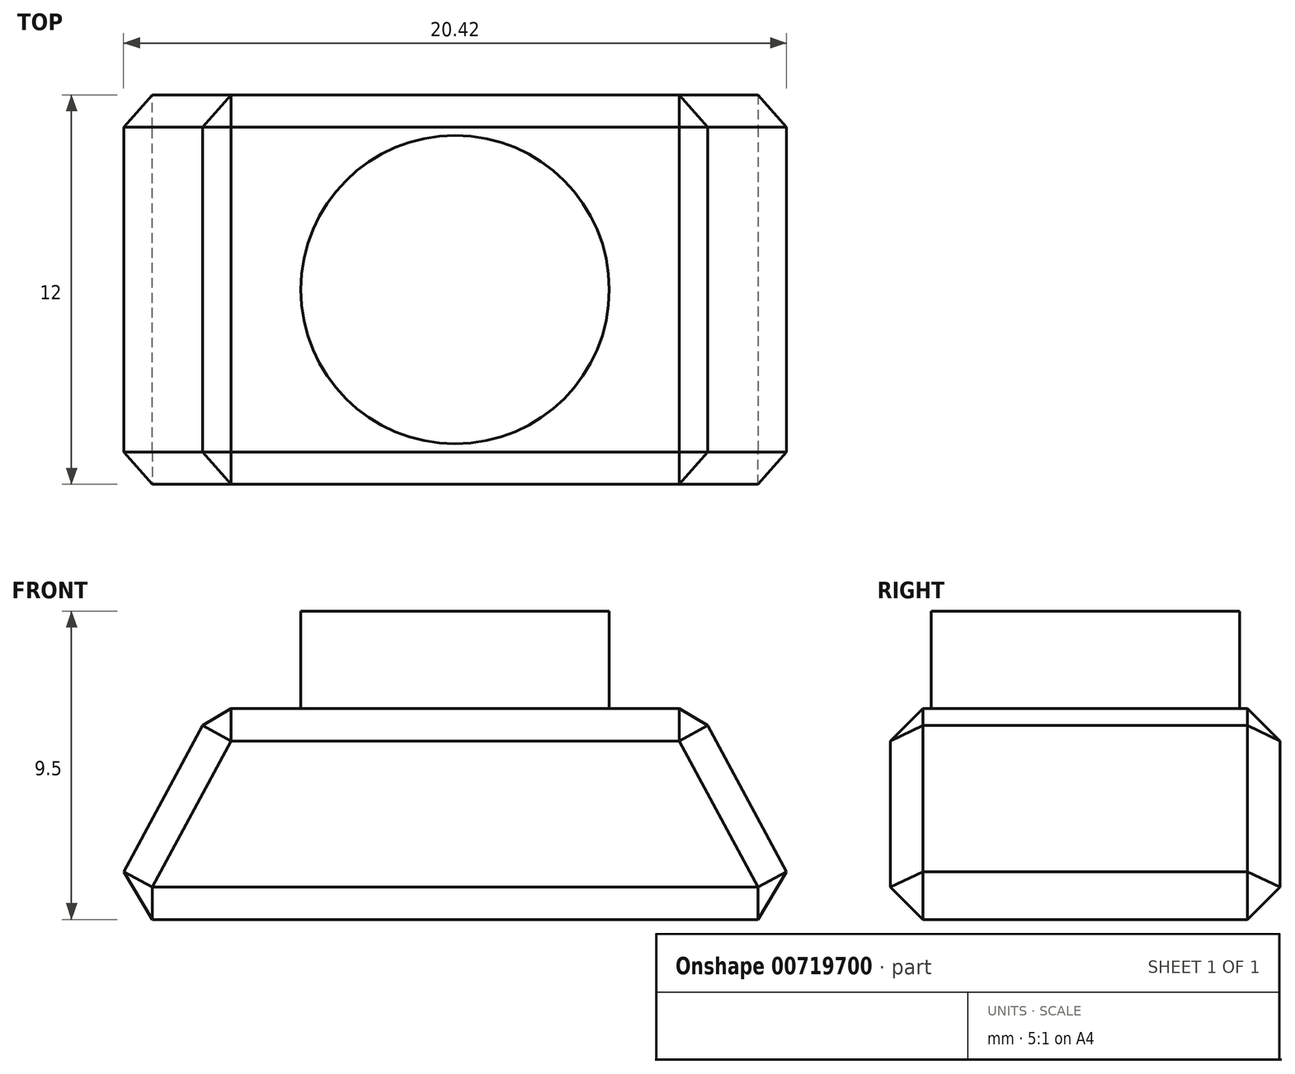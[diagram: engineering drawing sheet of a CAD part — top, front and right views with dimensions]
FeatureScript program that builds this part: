
annotation { "Feature Type Name" : "Feature", "Feature Type Description" : "" }
export const myFeature = defineFeature(function(context is Context, id is Id, definition is map)
    precondition{}
    {
        {
            var Q0;
            Q0=qCreatedBy(makeId("Top.planeOp"),FACE);
            var sketch = newSketch(context, id + "F0", { "sketchPlane" : qUnion([Q0])});
            skLineSegment(sketch, "E0.bottom", {"start": v(7.5, -6) * mm, "end": v(-7.5, -6) * mm});
            skLineSegment(sketch, "E0.top", {"start": v(7.5, 6) * mm, "end": v(-7.5, 6) * mm});
            skLineSegment(sketch, "E0.left", {"start": v(7.5, -6) * mm, "end": v(7.5, 6) * mm});
            skLineSegment(sketch, "E0.right", {"start": v(-7.5, -6) * mm, "end": v(-7.5, 6) * mm});
            skPoint(sketch, "E0.middle", {"position": v(0, 0) * mm});
            skCircle(sketch, "E1", {"center": v(0, 0) * mm, "radius": 4.75 * mm});
            skSolve(sketch);
        }
        {
            var Q0;
            Q0=makeQuery(id+"F0.imprint","IMPRINT",FACE,{"disambiguationData":[TD([[makeQuery(id+"F0.imprint","IMPRINT",EDGE,{"derivedFrom":sQuery(id+"F0.wireOp",EDGE,"E1")}),1.0]])]});
            extrude(context, id + "F1", {"entities" : qUnion([Q0]), "depth" : 3 * mm, "offsetDistance" : 25 * mm});
        }
        {
            var Q0;
            Q0=makeQuery(id+"F0.imprint","IMPRINT",FACE,{"disambiguationData":[TD([[makeQuery(id+"F0.imprint","IMPRINT",EDGE,{"derivedFrom":sQuery(id+"F0.wireOp",EDGE,"E0.bottom")}),-1.0]])]});
            cPlane(context, id + "F2", {"entities" : qUnion([Q0]), "cplaneType" : CPlaneType.OFFSET, "offset" : 6.5 * mm, "oppositeDirection" : true, "width" : 150 * mm, "height" : 150 * mm});
        }
        {
            var Q0;
            Q0=qCreatedBy(id+"F2.planeOp",FACE);
            var sketch = newSketch(context, id + "F3", { "sketchPlane" : qUnion([Q0])});
            skLineSegment(sketch, "E2.bottom", {"start": v(11, 6) * mm, "end": v(-11, 6) * mm});
            skLineSegment(sketch, "E2.top", {"start": v(11, -6) * mm, "end": v(-11, -6) * mm});
            skLineSegment(sketch, "E2.left", {"start": v(11, 6) * mm, "end": v(11, -6) * mm});
            skLineSegment(sketch, "E2.right", {"start": v(-11, 6) * mm, "end": v(-11, -6) * mm});
            skPoint(sketch, "E2.middle", {"position": v(0, 0) * mm});
            skSolve(sketch);
        }
        {
            var Q0;
            Q0=makeQuery(id+"F0.imprint","IMPRINT",FACE,{"disambiguationData":[TD([[makeQuery(id+"F0.imprint","IMPRINT",EDGE,{"derivedFrom":sQuery(id+"F0.wireOp",EDGE,"E1")}),1.0]])]});
            var sketch = newSketch(context, id + "F4", { "sketchPlane" : qUnion([Q0])});
            skLineSegment(sketch, "E3.bottom", {"start": v(7.5, 6) * mm, "end": v(-7.5, 6) * mm});
            skLineSegment(sketch, "E3.top", {"start": v(7.5, -6) * mm, "end": v(-7.5, -6) * mm});
            skLineSegment(sketch, "E3.left", {"start": v(7.5, 6) * mm, "end": v(7.5, -6) * mm});
            skLineSegment(sketch, "E3.right", {"start": v(-7.5, 6) * mm, "end": v(-7.5, -6) * mm});
            skPoint(sketch, "E3.middle", {"position": v(0, 0) * mm});
            skSolve(sketch);
        }
        {
            var Q1;
            Q1 = qSketchRegion(id + "F4", true);
            var Q2;
            Q2 = qSketchRegion(id + "F3", true);
            loft(context, id + "F5", {"operationType" : NewBodyOperationType.ADD, "sheetProfilesArray" : [{ "sheetProfileEntities" : qUnion([Q1]) }, { "sheetProfileEntities" : qUnion([Q2]) }]});
        }
        {
            var Q0;
            Q0=makeQuery(id+"F5.opLoft","SWEPT_FACE",FACE,{"disambiguationData":[OSD([sQuery(id+"F3.wireOp",EDGE,"E2.top"),sQuery(id+"F3.wireOp",EDGE,"E2.left"),sQuery(id+"F3.wireOp",EDGE,"E2.right"),sQuery(id+"F4.wireOp",EDGE,"E3.top"),sQuery(id+"F4.wireOp",EDGE,"E3.left"),sQuery(id+"F4.wireOp",EDGE,"E3.right")])]});
            var Q1;
            Q1=makeQuery(id+"F5.opLoft","SWEPT_FACE",FACE,{"disambiguationData":[OSD([sQuery(id+"F3.wireOp",EDGE,"E2.bottom"),sQuery(id+"F3.wireOp",EDGE,"E2.top"),sQuery(id+"F3.wireOp",EDGE,"E2.right"),sQuery(id+"F4.wireOp",EDGE,"E3.bottom"),sQuery(id+"F4.wireOp",EDGE,"E3.top"),sQuery(id+"F4.wireOp",EDGE,"E3.right")])]});
            var Q2;
            Q2=makeQuery(id+"F5.opLoft","SWEPT_FACE",FACE,{"disambiguationData":[OSD([sQuery(id+"F3.wireOp",EDGE,"E2.bottom"),sQuery(id+"F3.wireOp",EDGE,"E2.left"),sQuery(id+"F3.wireOp",EDGE,"E2.right"),sQuery(id+"F4.wireOp",EDGE,"E3.bottom"),sQuery(id+"F4.wireOp",EDGE,"E3.left"),sQuery(id+"F4.wireOp",EDGE,"E3.right")])]});
            var Q3;
            Q3=makeQuery(id+"F5.opLoft","SWEPT_FACE",FACE,{"disambiguationData":[OSD([sQuery(id+"F3.wireOp",EDGE,"E2.bottom"),sQuery(id+"F3.wireOp",EDGE,"E2.top"),sQuery(id+"F3.wireOp",EDGE,"E2.left"),sQuery(id+"F4.wireOp",EDGE,"E3.bottom"),sQuery(id+"F4.wireOp",EDGE,"E3.top"),sQuery(id+"F4.wireOp",EDGE,"E3.left")])]});
            chamfer(context, id + "F6", {"entities" : qUnion([Q0, Q1, Q2, Q3]), "width" : 1 * mm, "tangentPropagation" : true});
        }
    });
